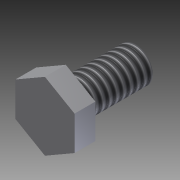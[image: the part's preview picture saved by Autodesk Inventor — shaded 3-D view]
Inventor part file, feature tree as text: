
AUTODESK INVENTOR PART (.ipt)
format: ipt  version: 2011 (Build 150239000, 239)  size: 85,504 bytes
history: native  units: in
note: dims shown in document units (in); Inventor stores cm internally (conversion verified against a paired STEP export)
features: extrude x2, sketch x2, thread x1
ambient origin geometry x8: Origin, YZ Plane, XZ Plane, XY Plane, X Axis, Y Axis, Z Axis, Center Point
bodies: Solid1 (feature_tree)
feature tree (5):
  extrude  "Extrusion1"  Depth=0.5in TaperAngle=0.0deg
  extrude  "Extrusion2"  Depth=0.15in TaperAngle=0.0deg
  thread  "Thread1"  [1 undecoded]
  sketch  "Sketch1"  dims[d0=0.25in d1=0.5in d2=0.0in]
  sketch  "Sketch2"  dims[d3=0.425in d4=0.15in d5=0.0in d6=1.0in d7=0.0in]
note: 1 required parameter value undecoded (feature->parameter linkage not recoverable at this tier; creation-order binding heuristic only, values carry confidence <= 0.55)
